# Revit family: spot_21_51se62mbb5b
name_source: partatom
category: Lighting Fixtures
units: mm (PartAtom-declared; Revit-internal decimal feet)

## family parameters
Cut with Voids When Loaded = No
Host = Face
Light Source = No
Part Type = Normal
Room Calculation Point = No
Round Connector Dimension = Use Diameter
Shared = No

## types (1)
- --- (1 x LED, 5300 lm, 41.7 W, 3000K)
    Apparent Load = 42 VA
    CIE Flux Codes = 95 98 99 100 100
    Color Rendering = 90
    Color Temperature = 3000K
    Default Elevation = 1800 mm
    Description = Spot 21, directional spotlight, light control with lens, of PMMA, LED rated luminous flux: 5.100lm, light colour: 930, control gear: ECG Multilumen, with 3-phase adapter, mains connection: 220..240V, AC, 50/60Hz, of aluminium, metallic grey (RAL 9006), length: 213mm, diameter: 105mm, protection rating (complete): IP20, insulation class (complete): insulation class I (protective earthing), certification: CE, impact resistance: IK02, permissible ambient temperature for indoor applications: -20..+40°C, packaging unit: 1 piece
    Height = 175 mm
    Lamp = 1 x LED
    Lamp Light Flux = 5300 lm
    Lamp Power = 41.7 W
    Lamp count = 1
    Length = 105 mm
    Luminous efficacy = 127 lm/W
    Manufacturer = Siteco
    ModVariant = No
    Model = 51SE62MBB5B
    Mounting Place = Ceiling
    Mounting Type = Pendant
    Number of Poles = 1
    OnlyDefault = Yes
    Power Factor = 1
    Product Name = Spot 21
    Product group = directional spotlight
    ProductGroupID = 905
    Protection Class = Protection class I
    Protection Degree = IP 20
    RLX_Detail_Level = 1
    RLX_Emergency_Light_Flux = 0 lm
    RLX_Emergency_Type = 0
    RLX_Emergency_Type_DB = No
    RlxData = <blob elided: 6017 chars, md5=9f5a158a>
    Socket = socket
    Standby Power = 0 W
    System Light Flux = 5300 lm
    System Power = 42 W
    Type Comments = factory setting: luminous flux: 100 % | (ON | ON | ON | ON) | 1050 mA
    URL = http://relux.com
    VarID = @adj_165729
    Voltage = 0 V
    Weight = 0.00 kg
    Width = 0 mm  [stored 0 ft]

note: [stored X ft] marks values corroborated as IEEE doubles in the binary element streams (Revit-internal decimal feet)

## geometry (parser evidence)
native form markers: Blend x2, Sweep x10
no freeform markers — native parametric forms only
